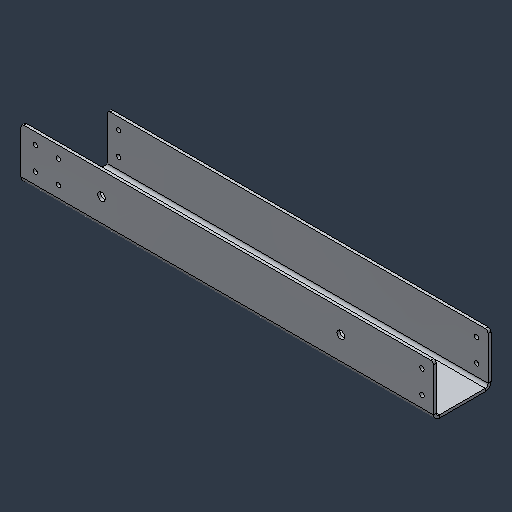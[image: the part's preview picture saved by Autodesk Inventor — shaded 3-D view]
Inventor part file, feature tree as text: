
AUTODESK INVENTOR PART (.ipt)
format: ipt  version: 2024.3 (Build 283343000, 343)  size: 131,584 bytes
history: native  units: mm (DEFAULTED — no unit token found)
features: fillet x1
ambient origin geometry x8: Origin, YZ Plane, XZ Plane, XY Plane, X Axis, Y Axis, Z Axis, Center Point
bodies: Solid1 (feature_tree)
feature tree (1):
  fillet  "Fillet1"  [1 undecoded]
note: 1 required parameter value undecoded (feature->parameter linkage not recoverable at this tier; creation-order binding heuristic only, values carry confidence <= 0.55)
